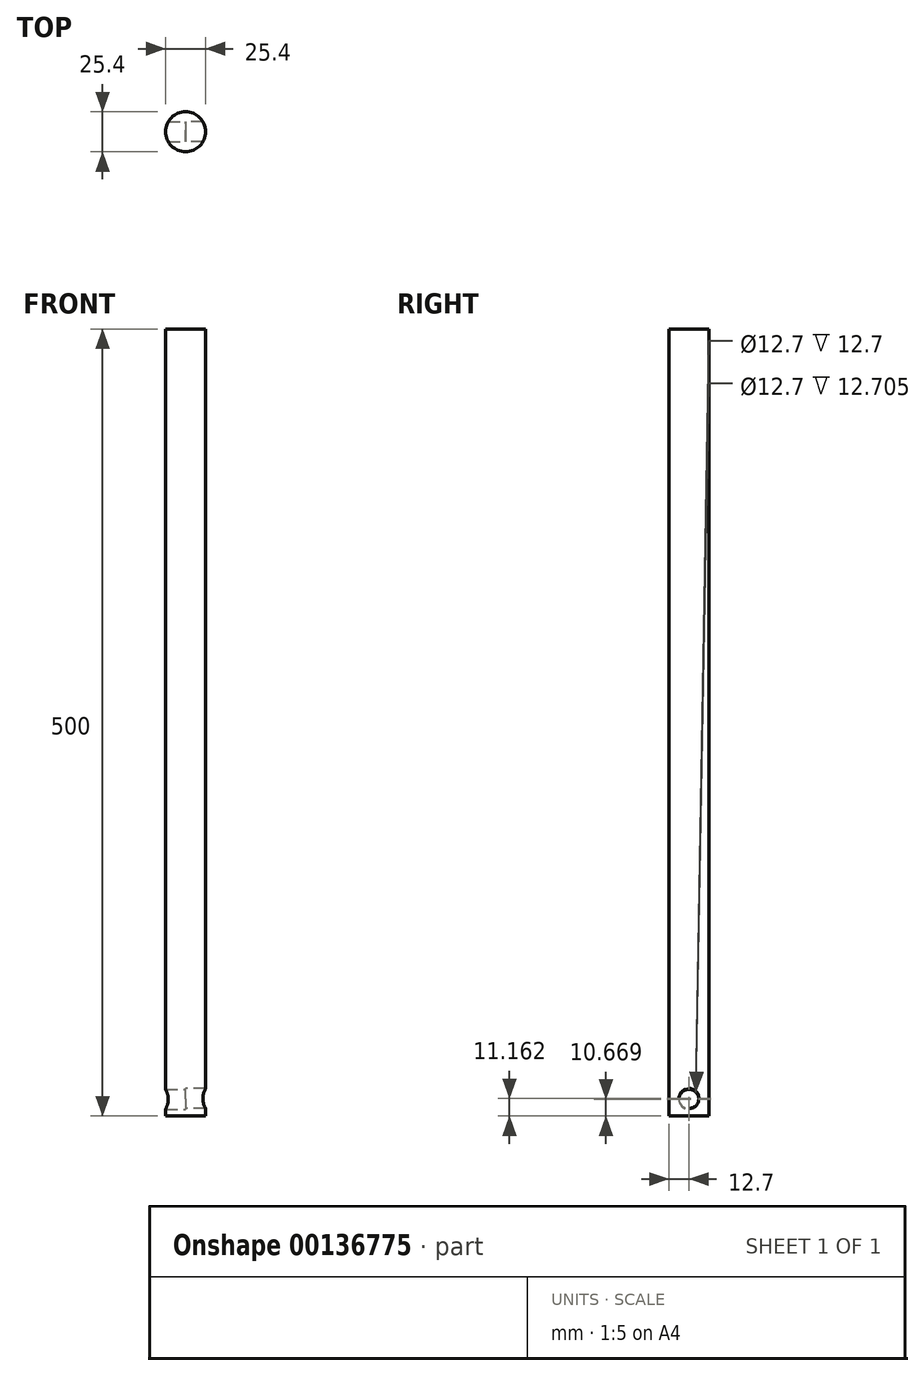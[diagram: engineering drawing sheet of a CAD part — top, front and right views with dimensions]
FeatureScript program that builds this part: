
annotation { "Feature Type Name" : "Feature", "Feature Type Description" : "" }
export const myFeature = defineFeature(function(context is Context, id is Id, definition is map)
    precondition{}
    {
        {
            var Q0;
            Q0=qCreatedBy(makeId("Top.planeOp"),FACE);
            var sketch = newSketch(context, id + "F0", { "sketchPlane" : qUnion([Q0])});
            skCircle(sketch, "E0", {"center": v(0, 0) * mm, "radius": 12.7 * mm});
            skSolve(sketch);
        }
        {
            var Q0;
            Q0 = qSketchRegion(id + "F0", true);
            extrude(context, id + "F1", {"entities" : qUnion([Q0]), "depth" : 500 * mm});
        }
        {
            var Q0;
            Q0=qCreatedBy(makeId("Right.planeOp"),FACE);
            var sketch = newSketch(context, id + "F2", { "sketchPlane" : qUnion([Q0])});
            skCircle(sketch, "E1", {"center": v(0, 11.16) * mm, "radius": 6.35 * mm});
            skSolve(sketch);
        }
        {
            var Q0;
            Q0 = qSketchRegion(id + "F2", true);
            extrude(context, id + "F3", {"entities" : qUnion([Q0]), "operationType" : NewBodyOperationType.REMOVE, "depth" : 76.2 * mm});
        }
        {
            var Q0;
            Q0=qCreatedBy(makeId("Right.planeOp"),FACE);
            var sketch = newSketch(context, id + "F4", { "sketchPlane" : qUnion([Q0])});
            skCircle(sketch, "E2", {"center": v(0, 10.67) * mm, "radius": 6.35 * mm});
            skSolve(sketch);
        }
        {
            var Q0;
            Q0 = qSketchRegion(id + "F4", true);
            extrude(context, id + "F5", {"entities" : qUnion([Q0]), "operationType" : NewBodyOperationType.REMOVE, "oppositeDirection" : true, "depth" : 76.2 * mm});
        }
    });
